# Revit family: Shower_Arm-American_Standard-Modern-1660.241.002
name_source: partatom
category: Pipe Accessories
revit_build: Autodesk Revit 2015 (Build: 20140606_1530(x64)
units: mm (PartAtom-declared; Revit-internal decimal feet)

## types (4) — shared parameters
Assembly Code = D2090800
Cold Water Connection Diameter = 1/2"
Cold Water Connection Radius = 1/4"
Default Elevation = 78"
Description = Modern
Flow Rate = 2.0 gpm (7.6 L/min)
Height = 2 3/16"
Hot Water Connection Diameter = 1"
Hot Water Connection Radius = 1/4"
Installation Type = Wall Mounted
Length = 5 1/2"
Manufacturer = American Standard
Price = Prices may vary. Please consult Manufacturer Representative for most up-to-date price list.
Product Documentation Link = https://www.americanstandard-us.com
Product Page URL = https://www.americanstandard-us.com
Tempered Connection Diameter = 1/2"
Tempered Connection Radius = 1/4"
URL = https://www.americanstandard-us.com
Warranty Documentation Link = https://www.americanstandard-us.com
Width = 2 1/2"

## per-type parameters (varying)
| type | Finish | Material |
| 1660.241.002 | Brass-American Standard-002-Chrome | Brass-American Standard-002-Chrome |
| 1660.241.295 | Brass-American Standard-295-Brushed Nickel | Brass-American Standard-295-Brushed Nickel |
| 1660.241.278 | Brass-American Standard-278-Legacy Bronze | Brass-American Standard-278-Legacy Bronze |
| 1660.241.013 | Brass-American Standard-013-Polished Nickel | Brass-American Standard-013-Polished Nickel |

note: column(s) folded — value = type name in every type: Model

## geometry (parser evidence)
native form markers: Sweep x3
no freeform markers — native parametric forms only
